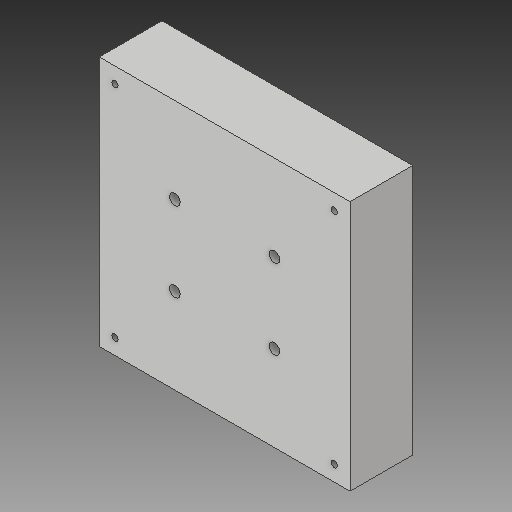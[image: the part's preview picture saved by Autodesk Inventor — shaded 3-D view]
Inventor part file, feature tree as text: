
AUTODESK INVENTOR PART (.ipt)
format: ipt  version: 2019 (Build 230136000, 136)  size: 130,560 bytes
history: native  units: in
note: dims shown in document units (in); Inventor stores cm internally (conversion verified against a paired STEP export)
features: sketch x3, hole x2, extrude x1
ambient origin geometry x8: Origin, YZ Plane, XZ Plane, XY Plane, X Axis, Y Axis, Z Axis, Center Point
bodies: Solid1 (feature_tree)
feature tree (6):
  extrude  "Extrusion1"  Depth=3.1496in
  hole  "Hole1"  [1 undecoded]
  hole  "Hole2"  [1 undecoded]
  sketch  "Sketch2"  dims[d0=3.1496in d1=3.1496in]
  sketch  "Sketch3"  dims[d2=0.7874in d3=0.0in d4=0.0984in]
  sketch  "Sketch4"  dims[d5=0.1969in d6=0.1969in d7=0.1969in d8=0.1969in d9=0.0984in d10=0.1969in d11=0.1969in d12=0.0984in d13=0.0793in d14=0.1969in d15=0.1575in d16=0.0787in d17=90.0deg d18=0.2992in d19=0.8108in d20=0.9498in d21=0.9498in d22=1.0748in d23=1.0748in d24=1.25in d25=1.25in d26=1.0in d27=1.0in d28=0.1181in d29=0.1181in d30=0.1181in d31=0.1181in d32=0.1339in d33=0.2362in d34=0.2362in d35=0.1969in d36=90.0deg d37=0.3465in d38=0.8108in d39=0.1969in d40=0.1969in]
note: 2 required parameter values undecoded (feature->parameter linkage not recoverable at this tier; creation-order binding heuristic only, values carry confidence <= 0.55)
